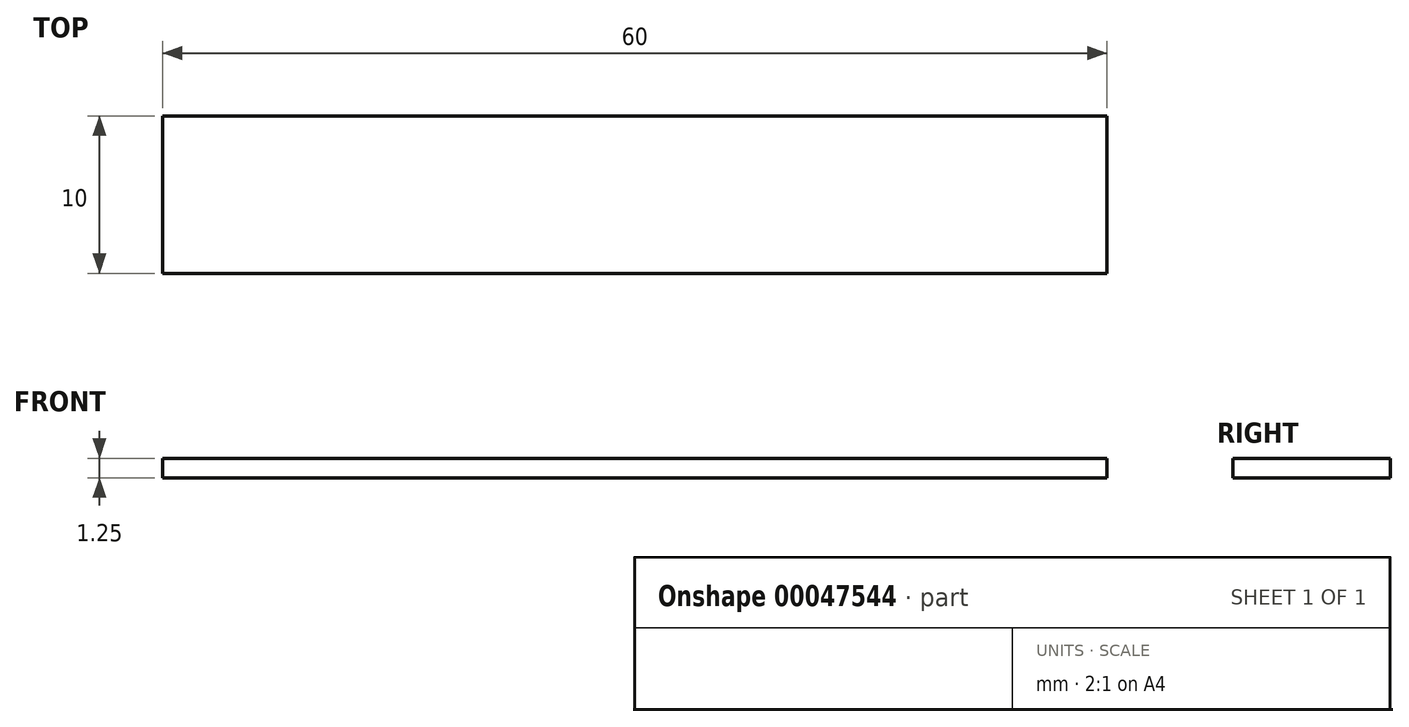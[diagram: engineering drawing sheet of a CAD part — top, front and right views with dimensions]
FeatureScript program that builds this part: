
annotation { "Feature Type Name" : "Feature", "Feature Type Description" : "" }
export const myFeature = defineFeature(function(context is Context, id is Id, definition is map)
    precondition{}
    {
        {
            var Q0;
            Q0=qCreatedBy(makeId("Top.planeOp"),FACE);
            var sketch = newSketch(context, id + "F0", { "sketchPlane" : qUnion([Q0])});
            skLineSegment(sketch, "E0.bottom", {"start": v(-30, 5) * mm, "end": v(30, 5) * mm});
            skLineSegment(sketch, "E0.top", {"start": v(-30, -5) * mm, "end": v(30, -5) * mm});
            skLineSegment(sketch, "E0.left", {"start": v(-30, 5) * mm, "end": v(-30, -5) * mm});
            skLineSegment(sketch, "E0.right", {"start": v(30, 5) * mm, "end": v(30, -5) * mm});
            skSolve(sketch);
        }
        {
            var Q0;
            Q0 = qSketchRegion(id + "F0", true);
            extrude(context, id + "F1", {"entities" : qUnion([Q0]), "depth" : 1.25 * mm});
        }
    });
